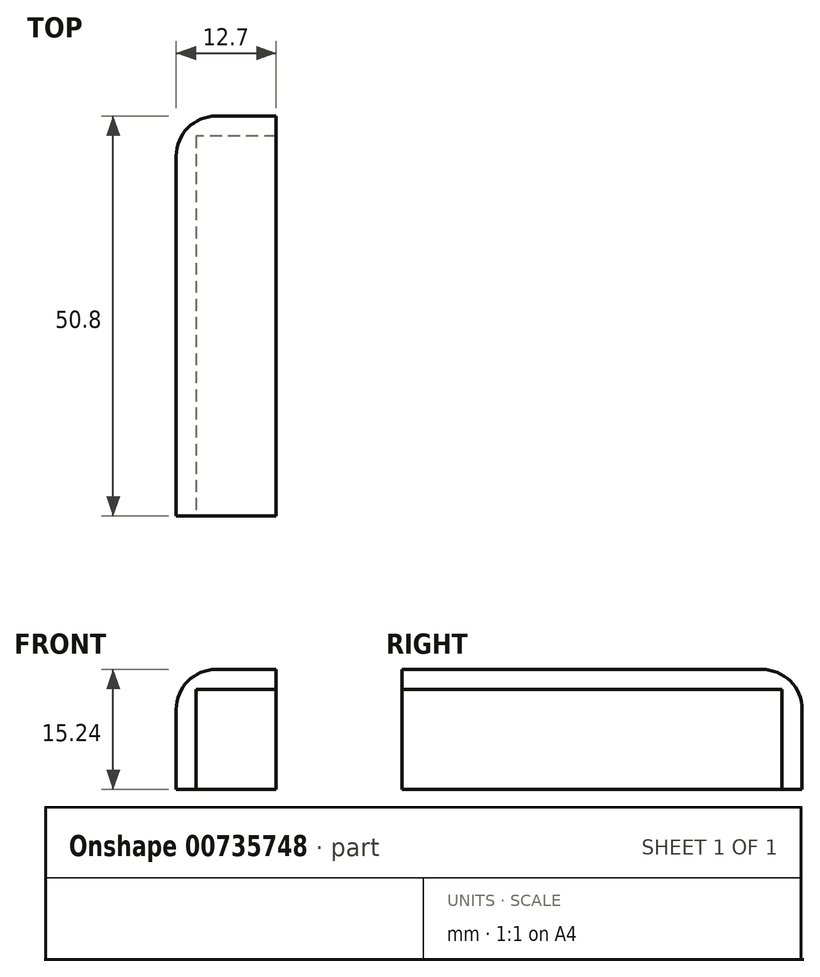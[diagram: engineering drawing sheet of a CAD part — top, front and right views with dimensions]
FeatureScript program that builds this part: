
annotation { "Feature Type Name" : "Feature", "Feature Type Description" : "" }
export const myFeature = defineFeature(function(context is Context, id is Id, definition is map)
    precondition{}
    {
        {
            var Q0;
            Q0=qCreatedBy(makeId("Top.planeOp"),FACE);
            var sketch = newSketch(context, id + "F0", { "sketchPlane" : qUnion([Q0])});
            skLineSegment(sketch, "E0", {"start": v(0, 0) * mm, "end": v(0, -50.8) * mm});
            skLineSegment(sketch, "E1", {"start": v(0, -50.8) * mm, "end": v(12.7, -50.8) * mm});
            skLineSegment(sketch, "E2", {"start": v(12.7, -50.8) * mm, "end": v(12.7, 0) * mm});
            skLineSegment(sketch, "E3", {"start": v(12.7, 0) * mm, "end": v(0, 0) * mm});
            skSolve(sketch);
        }
        {
            var Q0;
            Q0 = qSketchRegion(id + "F0", true);
            extrude(context, id + "F1", {"entities" : qUnion([Q0]), "depth" : 2.54 * mm, "offsetDistance" : 25.4 * mm});
        }
        {
            var Q0;
            Q0=makeQuery(id+"F1.opExtrude","CAP_FACE",FACE,{"disambiguationData":[OSD([sQuery(id+"F0.wireOp",EDGE,"E0"),sQuery(id+"F0.wireOp",EDGE,"E1"),sQuery(id+"F0.wireOp",EDGE,"E2"),sQuery(id+"F0.wireOp",EDGE,"E3")])],"isStart":true});
            var sketch = newSketch(context, id + "F2", { "sketchPlane" : qUnion([Q0])});
            skLineSegment(sketch, "E4", {"start": v(12.7, 0) * mm, "end": v(12.7, 2.54) * mm});
            skLineSegment(sketch, "E5", {"start": v(12.7, 2.54) * mm, "end": v(2.54, 2.54) * mm});
            skLineSegment(sketch, "E6", {"start": v(2.54, 2.54) * mm, "end": v(2.54, 50.8) * mm});
            skLineSegment(sketch, "E7", {"start": v(2.54, 50.8) * mm, "end": v(0, 50.8) * mm});
            skSolve(sketch);
        }
        {
            var Q0;
            Q0=makeQuery(id+"F2.imprint","IMPRINT",FACE,{"disambiguationData":[TD([[makeQuery(id+"F2.imprint","IMPRINT",EDGE,{"derivedFrom":sQuery(id+"F2.wireOp",EDGE,"E4")}),-1.0]])]});
            extrude(context, id + "F3", {"entities" : qUnion([Q0]), "operationType" : NewBodyOperationType.ADD, "depth" : 12.7 * mm, "offsetDistance" : 25.4 * mm});
        }
        {
            var Q0;
            {var subQ0=sQuery(id+"F0.wireOp",EDGE,"E3");var subQ1=sQuery(id+"F0.wireOp",EDGE,"E0");Q0=makeQuery(id+"F3.boolean.opBoolean","MERGE",EDGE,{"derivedFrom":[makeQuery(id+"F1.opExtrude","SWEPT_EDGE",EDGE,{"disambiguationData":[OSD([subQ1,subQ0])]}),makeQuery(id+"F3.opExtrude","SWEPT_EDGE",EDGE,{"disambiguationData":[OSD([subQ1,subQ0])]})]});}
            var Q1;
            Q1=makeQuery(id+"F1.opExtrude","CAP_EDGE",EDGE,{"disambiguationData":[OSD([sQuery(id+"F0.wireOp",EDGE,"E0")])],"isStart":false});
            var Q2;
            Q2=makeQuery(id+"F1.opExtrude","CAP_EDGE",EDGE,{"disambiguationData":[OSD([sQuery(id+"F0.wireOp",EDGE,"E3")])],"isStart":false});
            fillet(context, id + "F4", {"entities" : qUnion([Q0, Q1, Q2]), "radius" : 5.08 * mm, "tangentPropagation" : true, "allowEdgeOverflow" : false});
        }
    });
